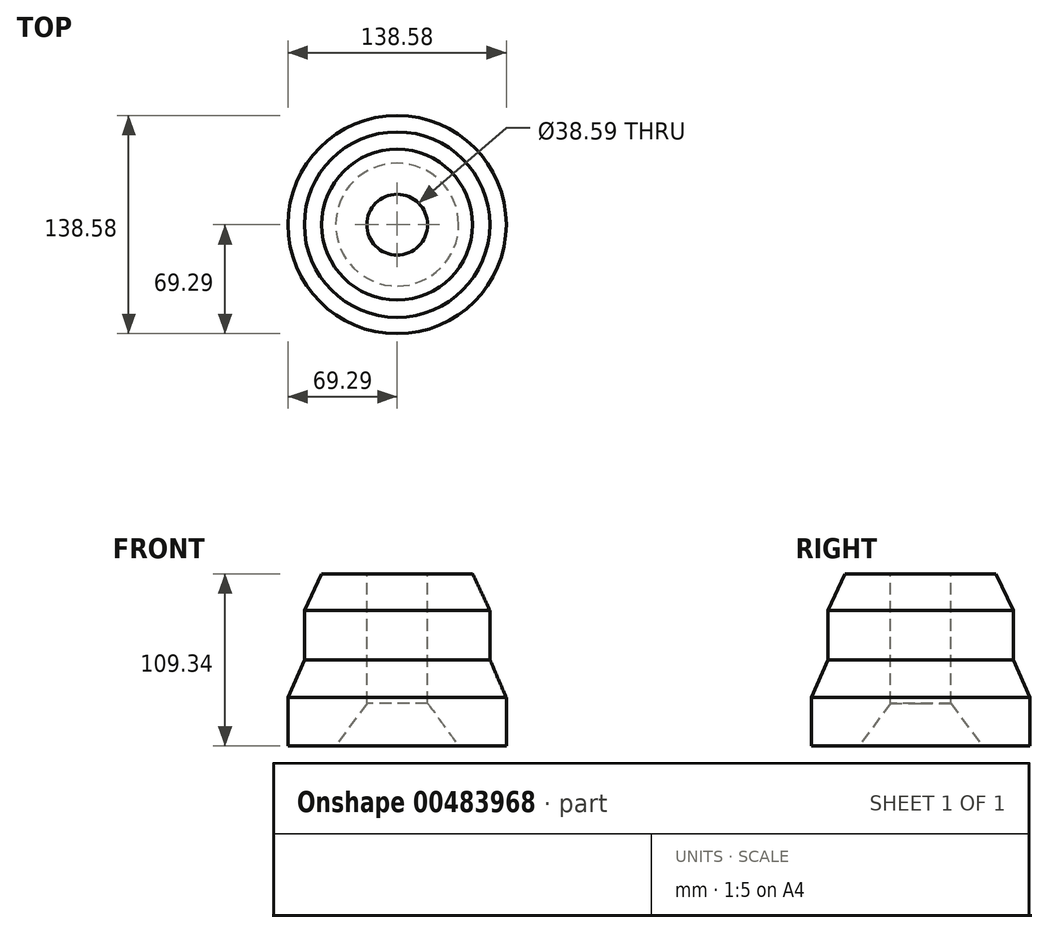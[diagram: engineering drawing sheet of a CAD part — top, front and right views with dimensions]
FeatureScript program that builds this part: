
annotation { "Feature Type Name" : "Feature", "Feature Type Description" : "" }
export const myFeature = defineFeature(function(context is Context, id is Id, definition is map)
    precondition{}
    {
        {
            var Q0;
            Q0=qCreatedBy(makeId("Front.planeOp"),FACE);
            var sketch = newSketch(context, id + "F0", { "sketchPlane" : qUnion([Q0])});
            skLineSegment(sketch, "E0", {"start": v(19.3, 54.56) * mm, "end": v(47.92, 54.56) * mm});
            skLineSegment(sketch, "E1", {"start": v(47.92, 54.56) * mm, "end": v(58.92, 31.33) * mm});
            skLineSegment(sketch, "E2", {"start": v(58.92, 31.33) * mm, "end": v(58.92, 0) * mm});
            skLineSegment(sketch, "E3", {"start": v(58.92, 0) * mm, "end": v(69.3, -24.07) * mm});
            skLineSegment(sketch, "E4", {"start": v(69.3, -24.07) * mm, "end": v(69.3, -54.78) * mm});
            skLineSegment(sketch, "E5", {"start": v(69.3, -54.78) * mm, "end": v(39, -54.78) * mm});
            skLineSegment(sketch, "E6", {"start": v(39, -54.78) * mm, "end": v(19.3, -27.6) * mm});
            skLineSegment(sketch, "E7", {"start": v(19.3, -27.6) * mm, "end": v(19.3, 54.56) * mm});
            skLineSegment(sketch, "E8", {"start": v(0, 94.6) * mm, "end": v(0, -86.92) * mm, "construction": true});
            skSolve(sketch);
        }
        {
            var Q0;
            Q0=makeQuery(id+"F0.imprint","IMPRINT",FACE,{"disambiguationData":[TD([[makeQuery(id+"F0.imprint","IMPRINT",EDGE,{"derivedFrom":sQuery(id+"F0.wireOp",EDGE,"E0")}),-1.0]])]});
            var Q1;
            Q1=sQuery(id+"F0.wireOp",EDGE,"E8");
            revolve(context, id + "F1", {"entities" : qUnion([Q0]), "axis" : qUnion([Q1]), "revolveType" : RevolveType.FULL});
        }
    });
